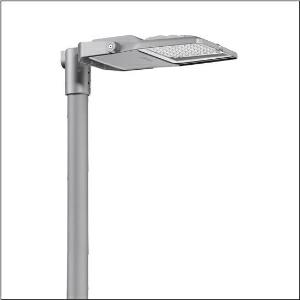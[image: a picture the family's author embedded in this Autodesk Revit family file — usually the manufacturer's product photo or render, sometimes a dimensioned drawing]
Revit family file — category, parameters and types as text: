
# Revit family: floodlight_fl_21_iq_mini___pl43_5xa7771d2a3a_a639
name_source: partatom
category: Lighting Fixtures
units: mm (PartAtom-declared; Revit-internal decimal feet)

## family parameters
Cut with Voids When Loaded = No
Host = Face
Light Source = No
Part Type = Normal
Room Calculation Point = No
Round Connector Dimension = Use Diameter
Shared = No

## types (1)
- --- (1 x LED, 18290 lm, 143 W, 3000K)
    Apparent Load = 143 VA
    CIE Flux Codes = 27 78 99 100 100
    Color Rendering = 70
    Color Temperature = 3000K
    Default Elevation = 1800 mm
    Description = Floodlight FL 21 iQ mini, floodlight, primary light control with lens, of PMMA, primary optical cover: protective disc, of toughened safety glass, transparent, light distribution: PL43, light emission: direct distribution, installation type: surface-mounted, LED, High Power LED, rated luminous flux: 18.290lm, luminous efficacy: 128lm/W, light colour: 730, colour temperature: 3000K, control: Auto-Match, Temp-Guard, Lumen-Switch, Night-Set, Smart-Wire, Light-Fading, Desk-Remote (wireless, voltage-free reading and setting of iQ features in the workshop via application-optimized NFC function/RFID function), optimised constant luminous flux control (CLO 2.0), with terminal, 6-pole, mains connection: 220..240V, AC, 50/60Hz, start of lifetime: 143W, end of service life: 152W, reduction: 61W, luminaire housing, of diecast aluminium, powder-coated, Siteco® metallic grey (DB 702S), corrosivity category C5 mid according to DIN EN ISO 12944, sealing non-destructively replaceable, please order mast flange separately, mast bracket, of steel, galvanised, powder-coated, Siteco® metallic grey (DB 702S), protection rating (complete): IP66, insulation class (complete): insulation class II (safety insulation), certification: CE, ENEC, VDE, protection symbol: D, impact resistance: IK08, permissible operating ambient temperature: -40..+40°C, permissible operating ambient temperature for outdoor applications: -40..+50°C, standard: DIN EN 12944, LABS conformity tested according to VDMA 24364:2018-05, packaging unit: 1 piece

Light Distribution: PL43
    Height = 70 mm
    Lamp = 1 x LED
    Lamp Light Flux = 18290 lm
    Lamp Power = 143 W
    Lamp count = 1
    Length = 485 mm
    Luminous efficacy = 128 lm/W
    Manufacturer = Siteco
    ModVariant = No
    Model = 5XA7771D2A3A
    Number of Poles = 1
    OnlyDefault = Yes
    Power Factor = 1
    Product Name = Floodlight FL 21 iQ mini | PL43
    Product group = floodlight | pylon annexe
    ProductGroupID = 6200
    Protection Class = Protection class II
    Protection Degree = IP 66
    RLX_Detail_Level = 1
    RLX_Emergency_Light_Flux = 0 lm
    RLX_Emergency_Type = 0
    RLX_Emergency_Type_DB = No
    RlxData = <blob elided: 101413 chars, md5=93ea7ed7>
    Socket = socket
    Standby Power = 0 W
    System Light Flux = 18290 lm
    System Power = 143 W
    Type Comments = factory setting: luminous flux: 100 % | dim-lin: 254 | 730 mA
    Type Image = l_1007125.jpg
    URL = http://relux.com
    VarID = @adj_094165
    Voltage = 0 V
    Weight = 0.00 kg
    Width = 337 mm

## geometry (parser evidence)
native form markers: Blend x4, Sweep x13
no freeform markers — native parametric forms only
